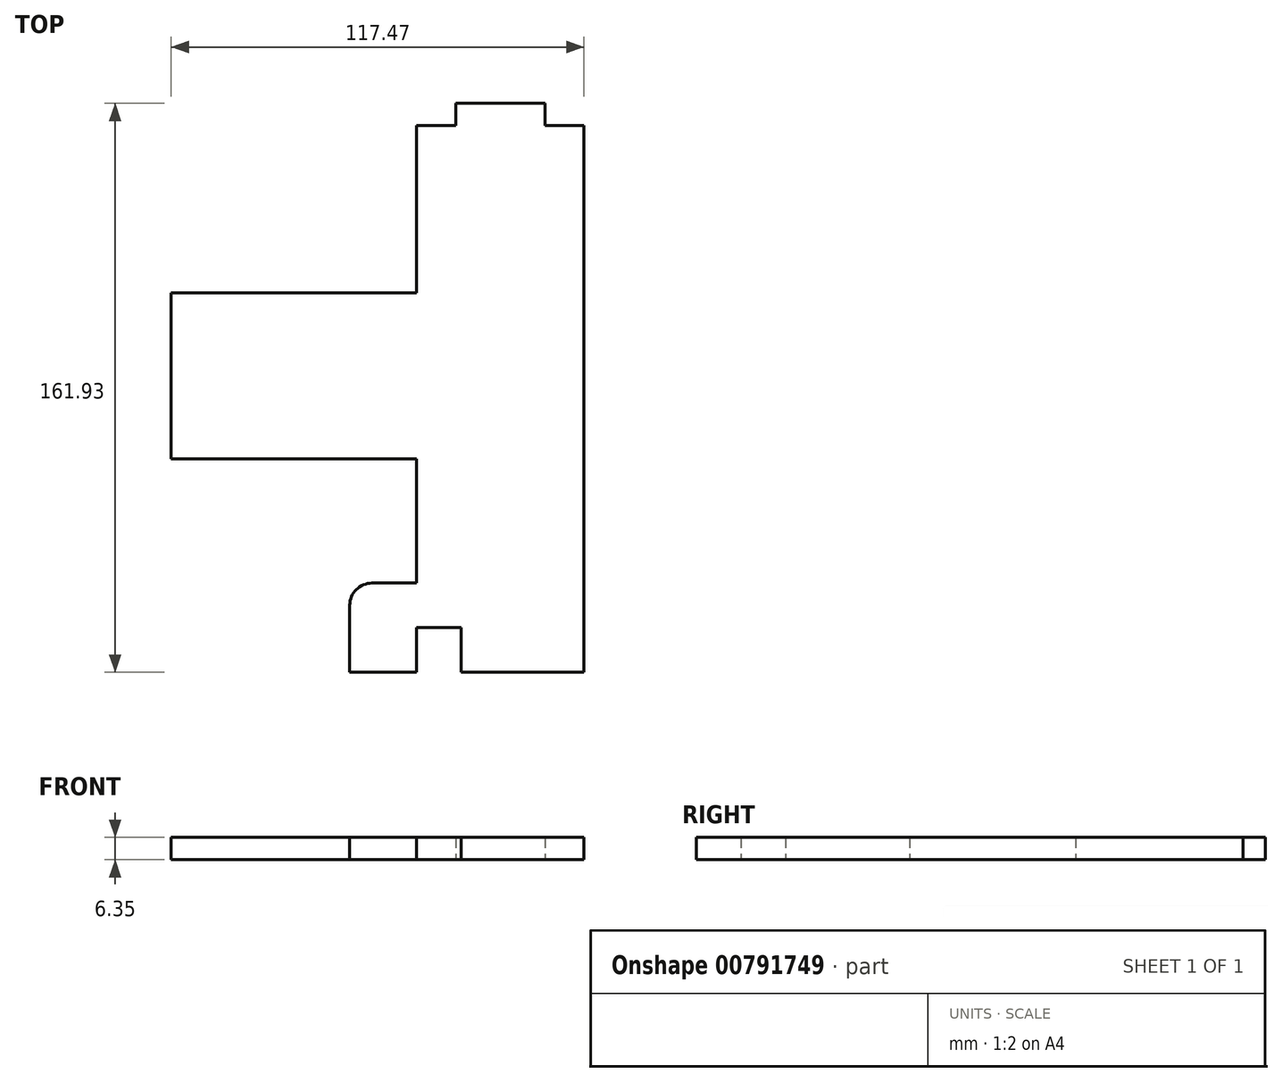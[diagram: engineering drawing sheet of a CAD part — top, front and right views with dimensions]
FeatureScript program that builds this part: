
annotation { "Feature Type Name" : "Feature", "Feature Type Description" : "" }
export const myFeature = defineFeature(function(context is Context, id is Id, definition is map)
    precondition{}
    {
        {
            var Q0;
            Q0=qCreatedBy(makeId("Top.planeOp"),FACE);
            var sketch = newSketch(context, id + "F0", { "sketchPlane" : qUnion([Q0])});
            skLineSegment(sketch, "E0", {"start": v(21.17, -220.11) * mm, "end": v(10.06, -220.11) * mm});
            skLineSegment(sketch, "E1", {"start": v(-26.45, -267.74) * mm, "end": v(-96.3, -267.74) * mm});
            skLineSegment(sketch, "E2", {"start": v(-96.3, -314.98) * mm, "end": v(-26.45, -314.98) * mm});
            skLineSegment(sketch, "E3", {"start": v(-26.45, -220.11) * mm, "end": v(-26.45, -267.74) * mm});
            skLineSegment(sketch, "E4", {"start": v(21.17, -220.11) * mm, "end": v(21.17, -375.69) * mm});
            skLineSegment(sketch, "E5", {"start": v(-13.75, -375.69) * mm, "end": v(21.17, -375.69) * mm});
            skLineSegment(sketch, "E6", {"start": v(-45.5, -356.64) * mm, "end": v(-45.5, -375.69) * mm});
            skLineSegment(sketch, "E7", {"start": v(-26.45, -362.99) * mm, "end": v(-13.75, -362.99) * mm});
            skLineSegment(sketch, "E8", {"start": v(-13.75, -375.69) * mm, "end": v(-13.75, -362.99) * mm});
            skLineSegment(sketch, "E9", {"start": v(-26.45, -350.29) * mm, "end": v(-39.15, -350.29) * mm});
            skLineSegment(sketch, "E10", {"start": v(-26.45, -375.69) * mm, "end": v(-45.5, -375.69) * mm});
            skLineSegment(sketch, "E11", {"start": v(-26.45, -362.99) * mm, "end": v(-26.45, -375.69) * mm});
            skLineSegment(sketch, "E12", {"start": v(-26.45, -314.98) * mm, "end": v(-26.45, -350.29) * mm});
            skLineSegment(sketch, "E13", {"start": v(-96.3, -267.74) * mm, "end": v(-96.3, -314.98) * mm});
            skPoint(sketch, "E14.visualSharp", {"position": v(-45.5, -350.29) * mm});
            skArc(sketch, "E14.filletArc", {"start": v(-39.15, -350.29) * mm, "mid": v(-43.64, -352.15) * mm, "end": v(-45.5, -356.64) * mm});
            skLineSegment(sketch, "E15.top", {"start": v(-15.34, -213.76) * mm, "end": v(10.06, -213.76) * mm});
            skLineSegment(sketch, "E15.left", {"start": v(-15.34, -220.11) * mm, "end": v(-15.34, -213.76) * mm});
            skLineSegment(sketch, "E15.right", {"start": v(10.06, -220.11) * mm, "end": v(10.06, -213.76) * mm});
            skLineSegment(sketch, "E16.trimOffspring", {"start": v(-15.34, -220.11) * mm, "end": v(-26.45, -220.11) * mm});
            skSolve(sketch);
        }
        {
            var Q0;
            Q0=qSketchRegion(id+"F0",true);
            extrude(context, id + "F1", {"entities" : qUnion([Q0]), "depth" : 6.35 * mm, "offsetDistance" : 25.4 * mm});
        }
    });
